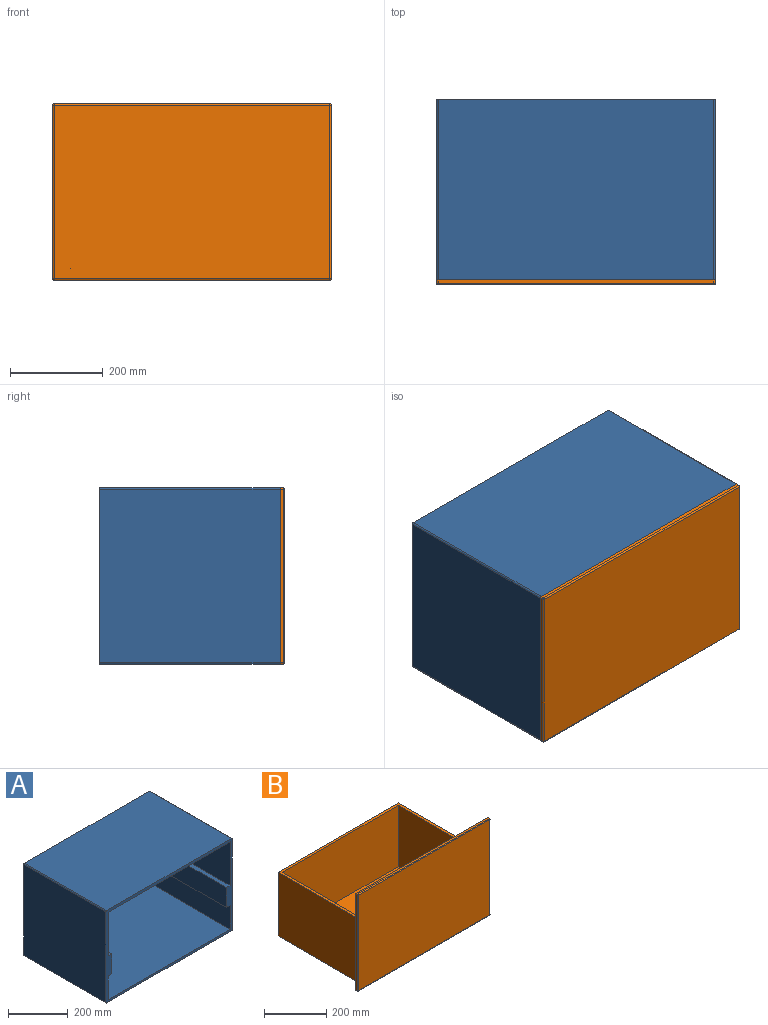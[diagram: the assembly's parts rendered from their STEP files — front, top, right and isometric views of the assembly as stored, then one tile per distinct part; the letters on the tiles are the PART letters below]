
ASSEMBLY  parts=2 mates=1
PART A: 23 faces, bbox 600x390x380 mm
  f0: plane 380x17.55mm, normal (0,0,1), area 6669.6mm2, adj f2,f3,f15,f18
  f1: plane 380x17.55mm, normal (0,0,-1), area 6669.6mm2, adj f2,f3,f4,f18
  f2: plane 380x82.2mm, normal (1,0,0), area 31235.9mm2, adj f0,f1,f3,f18
  f3: plane 600x380mm, normal (0,-1,0), area 22077.7mm2, adj f0,f1,f2,f4,f5,f6,f7,f8
  f4: plane 380x97.8mm, normal (1,0,0), area 37164.1mm2, adj f1,f3,f14,f18
  f5: plane 380x17.55mm, normal (0,0,-1), area 6669.6mm2, adj f3,f7,f8,f18
  f6: plane 380x17.55mm, normal (0,0,1), area 6669.6mm2, adj f3,f7,f17,f18
  f7: plane 380x82.2mm, normal (-1,0,0), area 31235.9mm2, adj f3,f5,f6,f18
  f8: plane 380x97.8mm, normal (-1,0,0), area 37164.1mm2, adj f3,f5,f14,f18
  f9: plane 390x374mm, normal (1,0,0), area 145860mm2, adj f3,f13,f19,f22
  f10: plane 594x390mm, normal (0,0,1), area 231660mm2, adj f3,f13,f19,f20
  f11: plane 390x374mm, normal (-1,0,0), area 145860mm2, adj f3,f13,f20,f21
  f12: plane 594x390mm, normal (0,0,-1), area 231660mm2, adj f3,f13,f21,f22
  f13: plane 600x380mm, normal (0,1,0), area 227992.3mm2, adj f9,f10,f11,f12,f19,f20,f21,f22
  f14: plane 580x380mm, normal (0,0,1), area 220400mm2, adj f3,f4,f8,f18
  f15: plane 380x180mm, normal (1,0,0), area 68400mm2, adj f0,f3,f16,f18
  f16: plane 580x380mm, normal (0,0,-1), area 220400mm2, adj f3,f15,f17,f18
  f17: plane 380x180mm, normal (-1,0,0), area 68400mm2, adj f3,f6,f16,f18
  f18: plane 580x360mm, normal (0,-1,0), area 205914.5mm2, adj f0,f1,f2,f4,f5,f6,f7,f8
  f19: cylinder r=3mm len=390mm, axis (0,-1,0), area 1837.8mm2, adj f3,f9,f10,f13
  f20: cylinder r=3mm len=390mm, axis (0,1,0), area 1837.8mm2, adj f3,f10,f11,f13
  f21: cylinder r=3mm len=390mm, axis (0,-1,0), area 1837.8mm2, adj f3,f11,f12,f13
  f22: cylinder r=3mm len=390mm, axis (0,1,0), area 1837.8mm2, adj f3,f9,f12,f13
PART B: 27 faces, bbox 600x390x380 mm
  f0: plane 600x380mm, normal (0,1,0), area 217743.3mm2, adj f1,f2,f3,f4,f6,f8,f11,f17
  f1: plane 374x7mm, normal (-1,0,0), area 2618mm2, adj f0,f11,f15,f17
  f2: plane 594x7mm, normal (0,0,-1), area 4158mm2, adj f0,f6,f10,f11
  f3: plane 374x7mm, normal (1,0,0), area 2618mm2, adj f0,f6,f8,f9
  f4: plane 594x7mm, normal (0,0,1), area 4158mm2, adj f0,f8,f14,f17
  f5: plane 594x374mm, normal (0,-1,0), area 222156mm2, adj f9,f10,f14,f15
  f6: cylinder r=3mm len=7mm, axis (0,1,0), area 33mm2, adj f0,f2,f3,f7
  f7: sphere r=3mm, area 14.1mm2, adj f6,f9,f10
  f8: cylinder r=3mm len=7mm, axis (0,-1,0), area 33mm2, adj f0,f3,f4,f12
  f9: cylinder r=3mm len=374mm, axis (0,0,1), area 1762.4mm2, adj f3,f5,f7,f12
  f10: cylinder r=3mm len=594mm, axis (1,0,0), area 2799.2mm2, adj f2,f5,f7,f13
  f11: cylinder r=3mm len=7mm, axis (0,-1,0), area 33mm2, adj f0,f1,f2,f13
  f12: sphere r=3mm, area 14.1mm2, adj f8,f9,f14
  f13: sphere r=3mm, area 14.1mm2, adj f10,f11,f15
  f14: cylinder r=3mm len=594mm, axis (-1,0,0), area 2799.2mm2, adj f4,f5,f12,f16
  f15: cylinder r=3mm len=374mm, axis (0,0,-1), area 1762.4mm2, adj f1,f5,f13,f16
  f16: sphere r=3mm, area 14.1mm2, adj f14,f15,f17
  f17: cylinder r=3mm len=7mm, axis (0,1,0), area 33mm2, adj f0,f1,f4,f16
  f18: plane 544.9x380mm, normal (0,0,-1), area 207060.9mm2, adj f0,f21,f25,f26
  f19: plane 544.9x380mm, normal (0,0,1), area 12849mm2, adj f0,f20,f21,f22,f23,f25,f26
  f20: plane 524.9x240mm, normal (0,-1,0), area 125975.3mm2, adj f19,f22,f23,f24
  f21: plane 544.9x250mm, normal (0,1,0), area 136224.3mm2, adj f18,f19,f25,f26
  f22: plane 370x240mm, normal (1,0,0), area 88800mm2, adj f0,f19,f20,f24
  f23: plane 370x240mm, normal (-1,0,0), area 88800mm2, adj f0,f19,f20,f24
  f24: plane 524.9x370mm, normal (0,0,1), area 194211.9mm2, adj f0,f20,f22,f23
  f25: plane 380x250mm, normal (-1,0,0), area 95000mm2, adj f0,f18,f19,f21
  f26: plane 380x250mm, normal (1,0,0), area 95000mm2, adj f0,f18,f19,f21
PLACE A t=(-42.29,-52.91,35.13)mm fixed
PLACE B t=(-42.29,-52.91,35.13)mm
MATE slider B.f5 <-> A.f13  axis (0,-1,0) through (220.16,-442.91,180.49)mm
